# Revit family: 706680001 Hand-Dryer_World-Dryer_SLIMdri
name_source: partatom
category: Aparatos eléctricos
revit_build: Autodesk Revit 2018 (Build: 20170223_1515(x64)
units: mm (PartAtom-declared; Revit-internal decimal feet)

## family parameters
Anfitrión = Cara
Compartido = No
Corte con vacíos al cargar = No
Cota de conector redondo = Diámetro de uso
Mantener orientación de anotación = No
Número OmniClass = 23.40.20.21.14
Punto de cálculo de habitación = No
Tipo de pieza = Normal
Título OmniClass = Hand and Hair Dryers

## types (1)
- 706680001 Hand-Dryer_World-Dryer_SLIMdri
    ADA Compliant = Sí
    Accionamiento = Sensor
    Actuation = as Specified
    Air Output = as Specified
    Air Temperature = as Specified
    Automatic = Sí
    Conexión electrica = Entrada 110 o 240 v
    Consumo de energía = 950 Watios
    Cover Material = <Por categoría>
    Código de montaje = C1030210
    Descripción = World Dryer Electric Hand Dryer as Specified
    Drying Time = as Specified
    Elevación por defecto = 1219 mm
    Expected Lifespan (Years) = 0
    Fabricante = World Dryer
    Frequency = 0 Hz
    Garantía = 10 años en el motor y carcasa  3 años en el ensamble del control
    Hardware Finish = Metal - World Dryer - Black
    MEP Amperage = 0 A
    MEP Apparent Power = 0 VA
    Maintenance Schedule (Months) = 0
    Manufacturer Website = http://www.worlddryer.com
    Marca = CORONA
    Material de fabricación = Carcasa en aluminio cepillado
    Modelo = As Specified
    Nombre = Secador Slim Max
    Nota clave = 10810
    Referencia = 706680001
    Revision = R1_7_2012
    Sound Pressure = 69 dB
    Standards Conformance = as Specified
    Surface Finish = Metal - World Dryer - White
    Tipo = Accesorio
    URL = https://www.corona.co
    Unit Depth = 99 mm
    Unit Length = 272 mm
    Unit Weight = 0
    Unit Width = 290 mm
    Vida útil ( ciclos ) = 500.000
    Voltage_MEP = 0 V
    Warranty Duration (Years) = 0

## geometry (parser evidence)
native form markers: Sweep x3
no freeform markers — native parametric forms only
